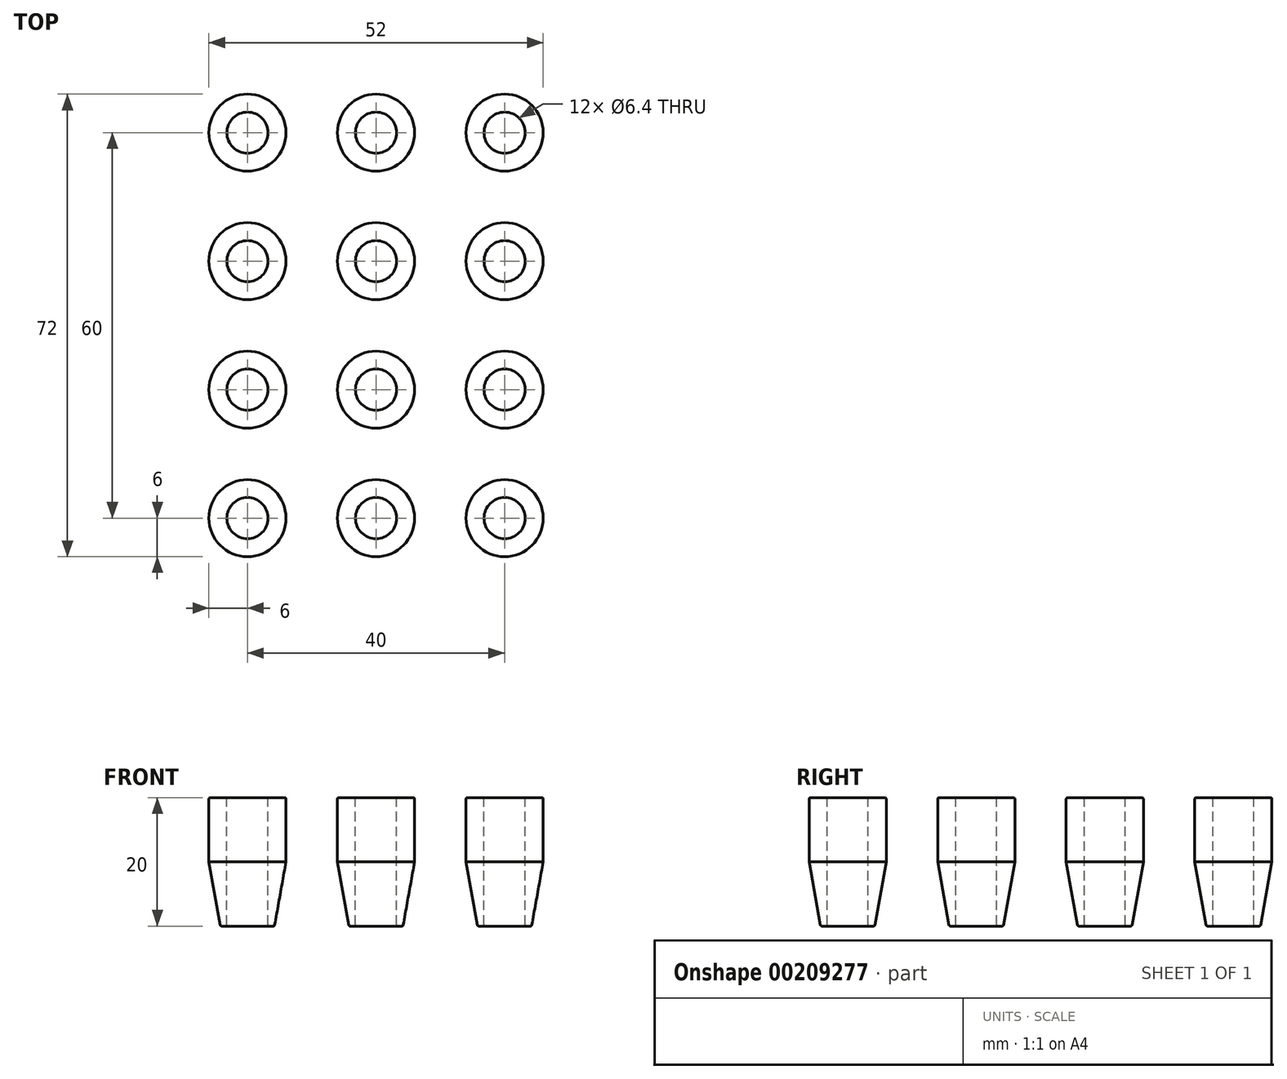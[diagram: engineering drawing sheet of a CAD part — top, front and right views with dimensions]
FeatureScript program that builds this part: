
annotation { "Feature Type Name" : "Feature", "Feature Type Description" : "" }
export const myFeature = defineFeature(function(context is Context, id is Id, definition is map)
    precondition{}
    {
        {
            var Q0;
            Q0=qCreatedBy(makeId("Front.planeOp"),FACE);
            var sketch = newSketch(context, id + "F0", { "sketchPlane" : qUnion([Q0])});
            skLineSegment(sketch, "E0", {"start": v(0, 0) * mm, "end": v(0, -10) * mm, "construction": true});
            skLineSegment(sketch, "E1", {"start": v(-3.2, -10) * mm, "end": v(-3.2, 0) * mm});
            skLineSegment(sketch, "E2", {"start": v(-3.2, -10) * mm, "end": v(-4.2, -10) * mm});
            skLineSegment(sketch, "E3", {"start": v(-4.2, -10) * mm, "end": v(-6, 0) * mm});
            skLineSegment(sketch, "E4.bottom", {"start": v(-3.2, 0) * mm, "end": v(-6, 0) * mm});
            skLineSegment(sketch, "E4.top", {"start": v(-3.2, 10) * mm, "end": v(-6, 10) * mm});
            skLineSegment(sketch, "E4.left", {"start": v(-3.2, 0) * mm, "end": v(-3.2, 10) * mm});
            skLineSegment(sketch, "E4.right", {"start": v(-6, 0) * mm, "end": v(-6, 10) * mm});
            skLineSegment(sketch, "E5", {"start": v(0, 0) * mm, "end": v(-3.2, 0) * mm, "construction": true});
            skSolve(sketch);
        }
        {
            var Q0;
            Q0=makeQuery(id+"F0.imprint","IMPRINT",FACE,{"disambiguationData":[TD([[makeQuery(id+"F0.imprint","IMPRINT",EDGE,{"derivedFrom":sQuery(id+"F0.wireOp",EDGE,"E4.bottom")}),-1.0]])]});
            var Q1;
            Q1=makeQuery(id+"F0.imprint","IMPRINT",FACE,{"disambiguationData":[TD([[makeQuery(id+"F0.imprint","IMPRINT",EDGE,{"derivedFrom":sQuery(id+"F0.wireOp",EDGE,"E1")}),1.0]])]});
            var Q2;
            Q2=sQuery(id+"F0.wireOp",EDGE,"E0");
            revolve(context, id + "F1", {"entities" : qUnion([Q0, Q1]), "axis" : qUnion([Q2]), "revolveType" : RevolveType.FULL});
        }
        {
            var Q0;
            Q0=makeQuery(id+"F1.opRevolve","SWEPT_EDGE",EDGE,{"disambiguationData":[OSD([sQuery(id+"F0.wireOp",EDGE,"E2"),sQuery(id+"F0.wireOp",EDGE,"E3")])]});
            var Q1;
            Q1=makeQuery(id+"F1.opRevolve","SWEPT_EDGE",EDGE,{"disambiguationData":[OSD([sQuery(id+"F0.wireOp",EDGE,"E4.top"),sQuery(id+"F0.wireOp",EDGE,"E4.right")])]});
            var Q2;
            Q2=makeQuery(id+"F1.opRevolve","SWEPT_EDGE",EDGE,{"disambiguationData":[OSD([sQuery(id+"F0.wireOp",EDGE,"E1"),sQuery(id+"F0.wireOp",EDGE,"E2")])]});
            fillet(context, id + "F2", {"entities" : qUnion([Q0, Q1, Q2]), "radius" : .2 * mm, "tangentPropagation" : true, "allowEdgeOverflow" : false});
        }
        {
            var Q0;
            Q0=makeQuery(id+"F1.opRevolve","SWEPT_BODY",BODY,{"disambiguationData":[OSD([sQuery(id+"F0.wireOp",EDGE,"E1"),sQuery(id+"F0.wireOp",EDGE,"E2"),sQuery(id+"F0.wireOp",EDGE,"E3"),sQuery(id+"F0.wireOp",EDGE,"E4.top"),sQuery(id+"F0.wireOp",EDGE,"E4.left"),sQuery(id+"F0.wireOp",EDGE,"E4.right")])]});
            transform(context, id + "F3", {"entities" : qUnion([Q0]), "transformType" : TransformType.TRANSLATION_3D, "dx" : 0 * mm, "dy" : -30 * mm, "dz" : 0 * mm, "makeCopy" : true});
        }
        {
            var Q0;
            Q0=makeQuery(id+"F1.opRevolve","SWEPT_BODY",BODY,{"disambiguationData":[OSD([sQuery(id+"F0.wireOp",EDGE,"E1"),sQuery(id+"F0.wireOp",EDGE,"E2"),sQuery(id+"F0.wireOp",EDGE,"E3"),sQuery(id+"F0.wireOp",EDGE,"E4.top"),sQuery(id+"F0.wireOp",EDGE,"E4.left"),sQuery(id+"F0.wireOp",EDGE,"E4.right")])]});
            deleteBodies(context, id + "F4", {"entities" : qUnion([Q0])});
        }
        {
            var Q0;
            Q0=makeQuery(id+"F3.opPattern","COPY",BODY,{"derivedFrom":makeQuery(id+"F1.opRevolve","SWEPT_BODY",BODY,{"disambiguationData":[OSD([sQuery(id+"F0.wireOp",EDGE,"E1"),sQuery(id+"F0.wireOp",EDGE,"E2"),sQuery(id+"F0.wireOp",EDGE,"E3"),sQuery(id+"F0.wireOp",EDGE,"E4.top"),sQuery(id+"F0.wireOp",EDGE,"E4.left"),sQuery(id+"F0.wireOp",EDGE,"E4.right")])]}),"instanceName":"1"});
            transform(context, id + "F5", {"entities" : qUnion([Q0]), "transformType" : TransformType.TRANSLATION_3D, "dx" : -20 * mm, "dy" : 0 * mm, "dz" : 0 * mm, "makeCopy" : true});
        }
        {
            var Q0;
            Q0=makeQuery(id+"F3.opPattern","COPY",BODY,{"derivedFrom":makeQuery(id+"F1.opRevolve","SWEPT_BODY",BODY,{"disambiguationData":[OSD([sQuery(id+"F0.wireOp",EDGE,"E1"),sQuery(id+"F0.wireOp",EDGE,"E2"),sQuery(id+"F0.wireOp",EDGE,"E3"),sQuery(id+"F0.wireOp",EDGE,"E4.top"),sQuery(id+"F0.wireOp",EDGE,"E4.left"),sQuery(id+"F0.wireOp",EDGE,"E4.right")])]}),"instanceName":"1"});
            transform(context, id + "F6", {"entities" : qUnion([Q0]), "transformType" : TransformType.TRANSLATION_3D, "dx" : 20 * mm, "dy" : 0 * mm, "dz" : 0 * mm, "makeCopy" : true});
        }
        {
            var Q0;
            Q0=makeQuery(id+"F5.opPattern","COPY",BODY,{"derivedFrom":makeQuery(id+"F3.opPattern","COPY",BODY,{"derivedFrom":makeQuery(id+"F1.opRevolve","SWEPT_BODY",BODY,{"disambiguationData":[OSD([sQuery(id+"F0.wireOp",EDGE,"E1"),sQuery(id+"F0.wireOp",EDGE,"E2"),sQuery(id+"F0.wireOp",EDGE,"E3"),sQuery(id+"F0.wireOp",EDGE,"E4.top"),sQuery(id+"F0.wireOp",EDGE,"E4.left"),sQuery(id+"F0.wireOp",EDGE,"E4.right")])]}),"instanceName":"1"}),"instanceName":"1"});
            transform(context, id + "F7", {"entities" : qUnion([Q0]), "transformType" : TransformType.TRANSLATION_3D, "dx" : 0 * mm, "dy" : 20 * mm, "dz" : 0 * mm, "makeCopy" : true});
        }
        {
            var Q0;
            Q0=makeQuery(id+"F3.opPattern","COPY",BODY,{"derivedFrom":makeQuery(id+"F1.opRevolve","SWEPT_BODY",BODY,{"disambiguationData":[OSD([sQuery(id+"F0.wireOp",EDGE,"E1"),sQuery(id+"F0.wireOp",EDGE,"E2"),sQuery(id+"F0.wireOp",EDGE,"E3"),sQuery(id+"F0.wireOp",EDGE,"E4.top"),sQuery(id+"F0.wireOp",EDGE,"E4.left"),sQuery(id+"F0.wireOp",EDGE,"E4.right")])]}),"instanceName":"1"});
            transform(context, id + "F8", {"entities" : qUnion([Q0]), "transformType" : TransformType.TRANSLATION_3D, "dx" : 0 * mm, "dy" : 20 * mm, "dz" : 0 * mm, "makeCopy" : true});
        }
        {
            var Q0;
            Q0=makeQuery(id+"F6.opPattern","COPY",BODY,{"derivedFrom":makeQuery(id+"F3.opPattern","COPY",BODY,{"derivedFrom":makeQuery(id+"F1.opRevolve","SWEPT_BODY",BODY,{"disambiguationData":[OSD([sQuery(id+"F0.wireOp",EDGE,"E1"),sQuery(id+"F0.wireOp",EDGE,"E2"),sQuery(id+"F0.wireOp",EDGE,"E3"),sQuery(id+"F0.wireOp",EDGE,"E4.top"),sQuery(id+"F0.wireOp",EDGE,"E4.left"),sQuery(id+"F0.wireOp",EDGE,"E4.right")])]}),"instanceName":"1"}),"instanceName":"1"});
            transform(context, id + "F9", {"entities" : qUnion([Q0]), "transformType" : TransformType.TRANSLATION_3D, "dx" : 0 * mm, "dy" : 20 * mm, "dz" : 0 * mm, "makeCopy" : true});
        }
        {
            var Q0;
            Q0=makeQuery(id+"F7.opPattern","COPY",BODY,{"derivedFrom":makeQuery(id+"F5.opPattern","COPY",BODY,{"derivedFrom":makeQuery(id+"F3.opPattern","COPY",BODY,{"derivedFrom":makeQuery(id+"F1.opRevolve","SWEPT_BODY",BODY,{"disambiguationData":[OSD([sQuery(id+"F0.wireOp",EDGE,"E1"),sQuery(id+"F0.wireOp",EDGE,"E2"),sQuery(id+"F0.wireOp",EDGE,"E3"),sQuery(id+"F0.wireOp",EDGE,"E4.top"),sQuery(id+"F0.wireOp",EDGE,"E4.left"),sQuery(id+"F0.wireOp",EDGE,"E4.right")])]}),"instanceName":"1"}),"instanceName":"1"}),"instanceName":"1"});
            transform(context, id + "F10", {"entities" : qUnion([Q0]), "transformType" : TransformType.TRANSLATION_3D, "dx" : 0 * mm, "dy" : 20 * mm, "dz" : 0 * mm, "makeCopy" : true});
        }
        {
            var Q0;
            Q0=makeQuery(id+"F8.opPattern","COPY",BODY,{"derivedFrom":makeQuery(id+"F3.opPattern","COPY",BODY,{"derivedFrom":makeQuery(id+"F1.opRevolve","SWEPT_BODY",BODY,{"disambiguationData":[OSD([sQuery(id+"F0.wireOp",EDGE,"E1"),sQuery(id+"F0.wireOp",EDGE,"E2"),sQuery(id+"F0.wireOp",EDGE,"E3"),sQuery(id+"F0.wireOp",EDGE,"E4.top"),sQuery(id+"F0.wireOp",EDGE,"E4.left"),sQuery(id+"F0.wireOp",EDGE,"E4.right")])]}),"instanceName":"1"}),"instanceName":"1"});
            transform(context, id + "F11", {"entities" : qUnion([Q0]), "transformType" : TransformType.TRANSLATION_3D, "dx" : 0 * mm, "dy" : 20 * mm, "dz" : 0 * mm, "makeCopy" : true});
        }
        {
            var Q0;
            Q0=makeQuery(id+"F9.opPattern","COPY",BODY,{"derivedFrom":makeQuery(id+"F6.opPattern","COPY",BODY,{"derivedFrom":makeQuery(id+"F3.opPattern","COPY",BODY,{"derivedFrom":makeQuery(id+"F1.opRevolve","SWEPT_BODY",BODY,{"disambiguationData":[OSD([sQuery(id+"F0.wireOp",EDGE,"E1"),sQuery(id+"F0.wireOp",EDGE,"E2"),sQuery(id+"F0.wireOp",EDGE,"E3"),sQuery(id+"F0.wireOp",EDGE,"E4.top"),sQuery(id+"F0.wireOp",EDGE,"E4.left"),sQuery(id+"F0.wireOp",EDGE,"E4.right")])]}),"instanceName":"1"}),"instanceName":"1"}),"instanceName":"1"});
            transform(context, id + "F12", {"entities" : qUnion([Q0]), "transformType" : TransformType.TRANSLATION_3D, "dx" : 0 * mm, "dy" : 20 * mm, "dz" : 0 * mm, "makeCopy" : true});
        }
        {
            var Q0;
            Q0=makeQuery(id+"F10.opPattern","COPY",BODY,{"derivedFrom":makeQuery(id+"F7.opPattern","COPY",BODY,{"derivedFrom":makeQuery(id+"F5.opPattern","COPY",BODY,{"derivedFrom":makeQuery(id+"F3.opPattern","COPY",BODY,{"derivedFrom":makeQuery(id+"F1.opRevolve","SWEPT_BODY",BODY,{"disambiguationData":[OSD([sQuery(id+"F0.wireOp",EDGE,"E1"),sQuery(id+"F0.wireOp",EDGE,"E2"),sQuery(id+"F0.wireOp",EDGE,"E3"),sQuery(id+"F0.wireOp",EDGE,"E4.top"),sQuery(id+"F0.wireOp",EDGE,"E4.left"),sQuery(id+"F0.wireOp",EDGE,"E4.right")])]}),"instanceName":"1"}),"instanceName":"1"}),"instanceName":"1"}),"instanceName":"1"});
            transform(context, id + "F13", {"entities" : qUnion([Q0]), "transformType" : TransformType.TRANSLATION_3D, "dx" : 0 * mm, "dy" : 20 * mm, "dz" : 0 * mm, "makeCopy" : true});
        }
        {
            var Q0;
            Q0=makeQuery(id+"F11.opPattern","COPY",BODY,{"derivedFrom":makeQuery(id+"F8.opPattern","COPY",BODY,{"derivedFrom":makeQuery(id+"F3.opPattern","COPY",BODY,{"derivedFrom":makeQuery(id+"F1.opRevolve","SWEPT_BODY",BODY,{"disambiguationData":[OSD([sQuery(id+"F0.wireOp",EDGE,"E1"),sQuery(id+"F0.wireOp",EDGE,"E2"),sQuery(id+"F0.wireOp",EDGE,"E3"),sQuery(id+"F0.wireOp",EDGE,"E4.top"),sQuery(id+"F0.wireOp",EDGE,"E4.left"),sQuery(id+"F0.wireOp",EDGE,"E4.right")])]}),"instanceName":"1"}),"instanceName":"1"}),"instanceName":"1"});
            transform(context, id + "F14", {"entities" : qUnion([Q0]), "transformType" : TransformType.TRANSLATION_3D, "dx" : 0 * mm, "dy" : 20 * mm, "dz" : 0 * mm, "makeCopy" : true});
        }
        {
            var Q0;
            Q0=makeQuery(id+"F12.opPattern","COPY",BODY,{"derivedFrom":makeQuery(id+"F9.opPattern","COPY",BODY,{"derivedFrom":makeQuery(id+"F6.opPattern","COPY",BODY,{"derivedFrom":makeQuery(id+"F3.opPattern","COPY",BODY,{"derivedFrom":makeQuery(id+"F1.opRevolve","SWEPT_BODY",BODY,{"disambiguationData":[OSD([sQuery(id+"F0.wireOp",EDGE,"E1"),sQuery(id+"F0.wireOp",EDGE,"E2"),sQuery(id+"F0.wireOp",EDGE,"E3"),sQuery(id+"F0.wireOp",EDGE,"E4.top"),sQuery(id+"F0.wireOp",EDGE,"E4.left"),sQuery(id+"F0.wireOp",EDGE,"E4.right")])]}),"instanceName":"1"}),"instanceName":"1"}),"instanceName":"1"}),"instanceName":"1"});
            transform(context, id + "F15", {"entities" : qUnion([Q0]), "transformType" : TransformType.TRANSLATION_3D, "dx" : 0 * mm, "dy" : 20 * mm, "dz" : 0 * mm, "makeCopy" : true});
        }
    });
